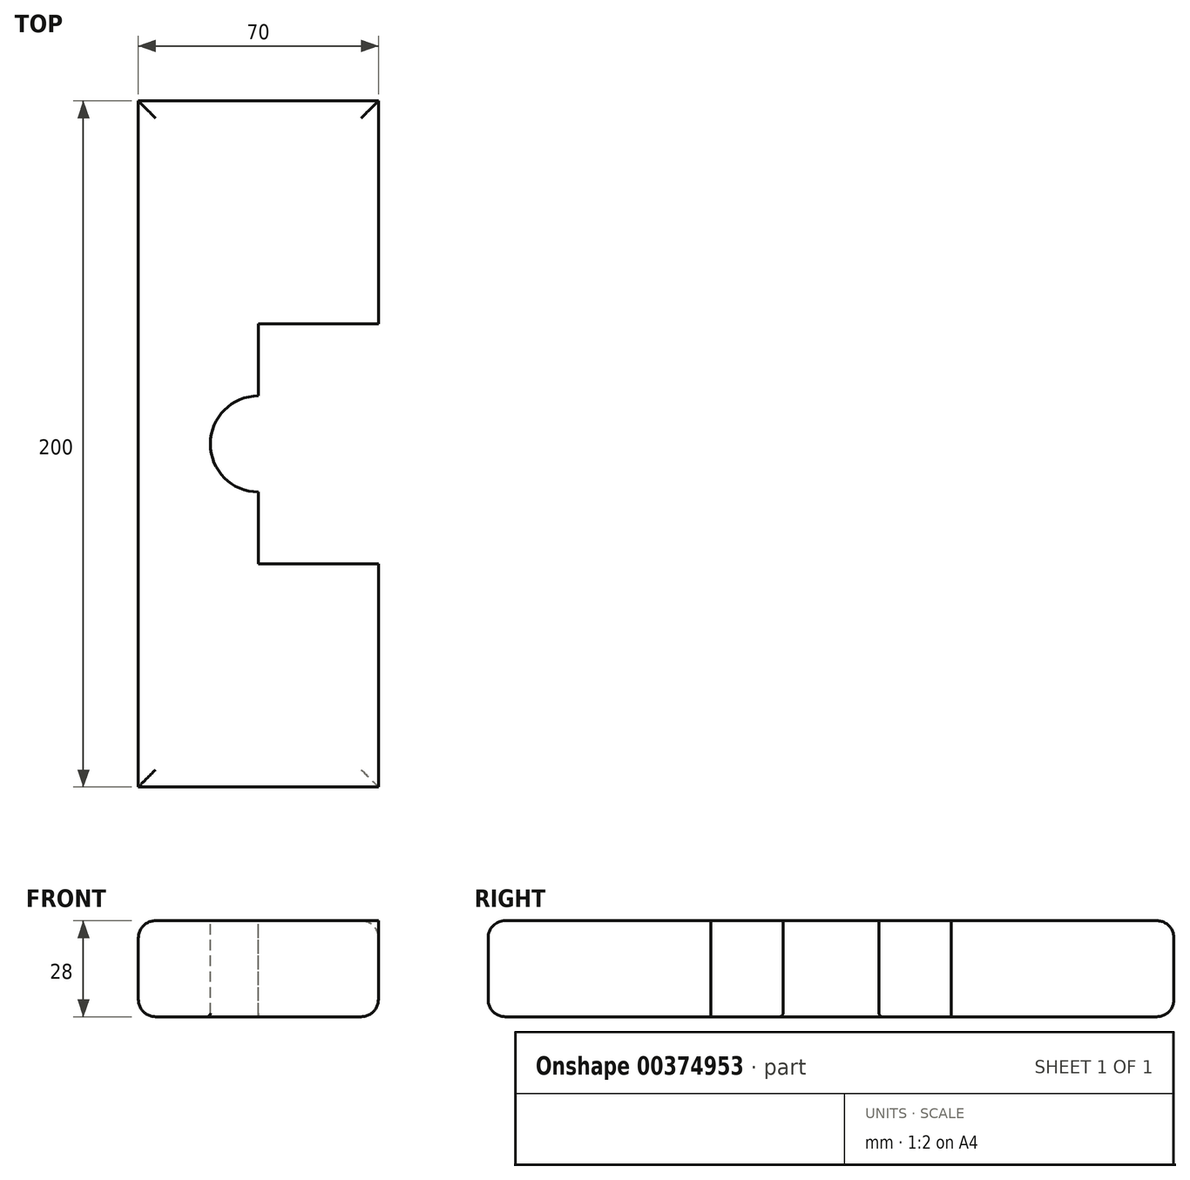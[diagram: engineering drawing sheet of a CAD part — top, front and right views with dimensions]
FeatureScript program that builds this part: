
annotation { "Feature Type Name" : "Feature", "Feature Type Description" : "" }
export const myFeature = defineFeature(function(context is Context, id is Id, definition is map)
    precondition{}
    {
        {
            var Q0;
            Q0=qCreatedBy(makeId("Front.planeOp"),FACE);
            var sketch = newSketch(context, id + "F0", { "sketchPlane" : qUnion([Q0])});
            skLineSegment(sketch, "E0.bottom", {"start": v(35, -14) * mm, "end": v(-35, -14) * mm});
            skLineSegment(sketch, "E0.top", {"start": v(35, 14) * mm, "end": v(-35, 14) * mm});
            skLineSegment(sketch, "E0.left", {"start": v(35, -14) * mm, "end": v(35, 14) * mm});
            skLineSegment(sketch, "E0.right", {"start": v(-35, -14) * mm, "end": v(-35, 14) * mm});
            skPoint(sketch, "E0.middle", {"position": v(0, 0) * mm});
            skSolve(sketch);
        }
        {
            var Q0;
            Q0 = qSketchRegion(id + "F0", true);
            extrude(context, id + "F1", {"entities" : qUnion([Q0]), "endBound" : BoundingType.SYMMETRIC, "depth" : 200 * mm});
        }
        {
            var Q0;
            Q0=makeQuery(id+"F1.opExtrude","SWEPT_FACE",FACE,{"disambiguationData":[OSD([sQuery(id+"F0.wireOp",EDGE,"E0.top")])]});
            var sketch = newSketch(context, id + "F2", { "sketchPlane" : qUnion([Q0])});
            skLineSegment(sketch, "E1.bottom", {"start": v(0, 35) * mm, "end": v(70, 35) * mm});
            skLineSegment(sketch, "E1.top", {"start": v(0, -35) * mm, "end": v(70, -35) * mm});
            skLineSegment(sketch, "E1.left", {"start": v(0, 35) * mm, "end": v(0, -35) * mm});
            skLineSegment(sketch, "E1.right", {"start": v(70, 35) * mm, "end": v(70, -35) * mm});
            skPoint(sketch, "E1.middle", {"position": v(35, 0) * mm});
            skSolve(sketch);
        }
        {
            var Q0;
            Q0 = qSketchRegion(id + "F2", true);
            extrude(context, id + "F3", {"entities" : qUnion([Q0]), "operationType" : NewBodyOperationType.REMOVE, "endBound" : BoundingType.THROUGH_ALL, "oppositeDirection" : true, "depth" : 25 * mm});
        }
        {
            var Q0;
            Q0=makeQuery(id+"F1.opExtrude","SWEPT_FACE",FACE,{"disambiguationData":[OSD([sQuery(id+"F0.wireOp",EDGE,"E0.top")])]});
            var sketch = newSketch(context, id + "F4", { "sketchPlane" : qUnion([Q0])});
            skCircle(sketch, "E2", {"center": v(0, 0) * mm, "radius": 14 * mm});
            skSolve(sketch);
        }
        {
            var Q0;
            Q0 = qSketchRegion(id + "F4", true);
            extrude(context, id + "F5", {"entities" : qUnion([Q0]), "operationType" : NewBodyOperationType.REMOVE, "endBound" : BoundingType.THROUGH_ALL, "oppositeDirection" : true, "depth" : 25 * mm});
        }
        {
            var Q0;
            Q0=makeQuery(id+"F1.opExtrude","SWEPT_EDGE",EDGE,{"disambiguationData":[OSD([sQuery(id+"F0.wireOp",EDGE,"E0.top"),sQuery(id+"F0.wireOp",EDGE,"E0.right")])]});
            var Q1;
            {var subQ0=sQuery(id+"F0.wireOp",EDGE,"E0.left");var subQ1=sQuery(id+"F0.wireOp",EDGE,"E0.top");Q1=makeQuery(id+"F3.boolean.opBoolean","SPLIT",EDGE,{"disambiguationData":[TD([makeQuery(id+"F3.opExtrude","SWEPT_FACE",FACE,{"disambiguationData":[OSD([sQuery(id+"F2.wireOp",EDGE,"E1.bottom")])]})])],"derivedFrom":makeQuery(id+"F1.opExtrude","SWEPT_EDGE",EDGE,{"disambiguationData":[OSD([subQ1,subQ0])]})});}
            var Q2;
            Q2=makeQuery(id+"F1.opExtrude","CAP_EDGE",EDGE,{"disambiguationData":[OSD([sQuery(id+"F0.wireOp",EDGE,"E0.top")])],"isStart":true});
            var Q3;
            Q3=makeQuery(id+"F1.opExtrude","CAP_EDGE",EDGE,{"disambiguationData":[OSD([sQuery(id+"F0.wireOp",EDGE,"E0.top")])],"isStart":false});
            var Q4;
            {var subQ0=sQuery(id+"F0.wireOp",EDGE,"E0.bottom");var subQ1=sQuery(id+"F0.wireOp",EDGE,"E0.left");Q4=makeQuery(id+"F3.boolean.opBoolean","SPLIT",EDGE,{"disambiguationData":[TD([makeQuery(id+"F3.opExtrude","SWEPT_FACE",FACE,{"disambiguationData":[OSD([sQuery(id+"F2.wireOp",EDGE,"E1.bottom")])]})])],"derivedFrom":makeQuery(id+"F1.opExtrude","SWEPT_EDGE",EDGE,{"disambiguationData":[OSD([subQ0,subQ1])]})});}
            var Q5;
            Q5=makeQuery(id+"F1.opExtrude","SWEPT_EDGE",EDGE,{"disambiguationData":[OSD([sQuery(id+"F0.wireOp",EDGE,"E0.bottom"),sQuery(id+"F0.wireOp",EDGE,"E0.right")])]});
            var Q6;
            {var subQ0=sQuery(id+"F0.wireOp",EDGE,"E0.bottom");var subQ1=sQuery(id+"F0.wireOp",EDGE,"E0.left");Q6=makeQuery(id+"F3.boolean.opBoolean","SPLIT",EDGE,{"disambiguationData":[TD([makeQuery(id+"F3.opExtrude","SWEPT_FACE",FACE,{"disambiguationData":[OSD([sQuery(id+"F2.wireOp",EDGE,"E1.top")])]})])],"derivedFrom":makeQuery(id+"F1.opExtrude","SWEPT_EDGE",EDGE,{"disambiguationData":[OSD([subQ0,subQ1])]})});}
            var Q7;
            Q7=makeQuery(id+"F1.opExtrude","CAP_EDGE",EDGE,{"disambiguationData":[OSD([sQuery(id+"F0.wireOp",EDGE,"E0.bottom")])],"isStart":false});
            var Q8;
            Q8=makeQuery(id+"F1.opExtrude","CAP_EDGE",EDGE,{"disambiguationData":[OSD([sQuery(id+"F0.wireOp",EDGE,"E0.bottom")])],"isStart":true});
            fillet(context, id + "F6", {"entities" : qUnion([Q0, Q1, Q2, Q3, Q4, Q5, Q6, Q7, Q8]), "radius" : 5 * mm, "tangentPropagation" : true, "allowEdgeOverflow" : false});
        }
        {
            var Q0;
            Q0=makeQuery(id+"F5.boolean.opBoolean","COPY",EDGE,{"derivedFrom":makeQuery(id+"F5.opExtrude","CAP_EDGE",EDGE,{"disambiguationData":[OSD([sQuery(id+"F4.wireOp",EDGE,"E2")])],"isStart":true})});
            var Q1;
            Q1=makeQuery(id+"F5.boolean.opBoolean","INTERSECT",EDGE,{"derivedFrom":[makeQuery(id+"F1.opExtrude","SWEPT_FACE",FACE,{"disambiguationData":[OSD([sQuery(id+"F0.wireOp",EDGE,"E0.bottom")])]}),makeQuery(id+"F5.opExtrude","SWEPT_FACE",FACE,{"disambiguationData":[OSD([sQuery(id+"F4.wireOp",EDGE,"E2")])]})]});
            fillet(context, id + "F7", {"entities" : qUnion([Q0, Q1]), "radius" : 1 * mm, "tangentPropagation" : true, "allowEdgeOverflow" : false});
        }
    });
